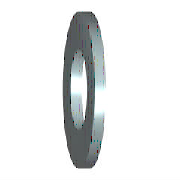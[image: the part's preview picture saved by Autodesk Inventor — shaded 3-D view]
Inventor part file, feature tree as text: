
AUTODESK INVENTOR PART (.ipt)
format: ipt  version: 2016 (Build 200138000, 138)  size: 108,032 bytes
history: native  units: mm (DEFAULTED — no unit token found)
features: other x1, plane x1, sketch x1
ambient origin geometry x7: Origin, YZ Plane, XY Plane, X Axis, Y Axis, Z Axis, Center Point
bodies: Solid1 (feature_tree), Body (feature_tree)
feature tree (3):
  other  "Work Axis1"
  plane  "Work Plane1"
  sketch  "Sketch"  dims[d0=1.1mm d1=2.5mm d2=0.3mm d3=0.0mm d4=0.0mm d5=0.0mm d6=0.0mm d7=0.0mm]
